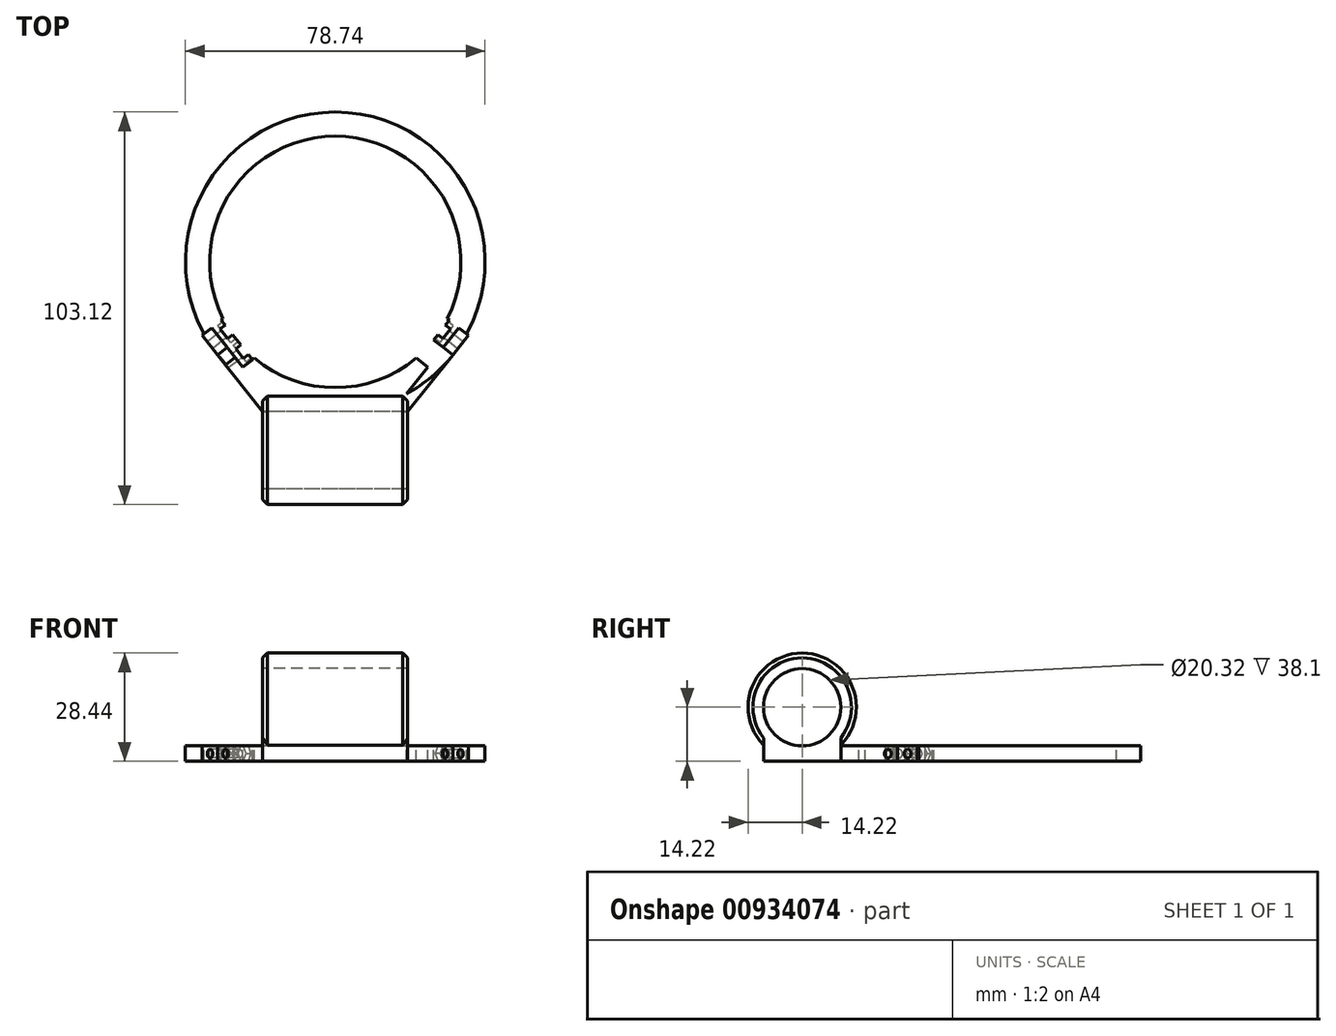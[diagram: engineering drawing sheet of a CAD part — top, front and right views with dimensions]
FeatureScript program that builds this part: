
annotation { "Feature Type Name" : "Feature", "Feature Type Description" : "" }
export const myFeature = defineFeature(function(context is Context, id is Id, definition is map)
    precondition{}
    {
        {
            var Q0;
            Q0=qCreatedBy(makeId("Top.planeOp"),FACE);
            var sketch = newSketch(context, id + "F0", { "sketchPlane" : qUnion([Q0])});
            skCircle(sketch, "E0", {"center": v(0, 0) * mm, "radius": 33.02 * mm});
            skCircle(sketch, "E1", {"center": v(0, 0) * mm, "radius": 39.37 * mm});
            skLineSegment(sketch, "E2", {"start": v(0, -39.37) * mm, "end": v(0, -59.7) * mm});
            skLineSegment(sketch, "E3", {"start": v(0, -59.7) * mm, "end": v(-19.05, -59.7) * mm});
            skLineSegment(sketch, "E4.bottom", {"start": v(-19.05, -59.7) * mm, "end": v(19.05, -59.7) * mm});
            skLineSegment(sketch, "E4.top", {"start": v(-19.05, -39.37) * mm, "end": v(19.05, -39.37) * mm});
            skLineSegment(sketch, "E4.left", {"start": v(-19.05, -59.7) * mm, "end": v(-19.05, -39.37) * mm});
            skLineSegment(sketch, "E4.right", {"start": v(19.05, -59.7) * mm, "end": v(19.05, -39.37) * mm});
            skPoint(sketch, "E4.middle", {"position": v(0, -49.53) * mm});
            skLineSegment(sketch, "E5", {"start": v(-19.05, -39.37) * mm, "end": v(-30.87, -24.43) * mm});
            skLineSegment(sketch, "E6", {"start": v(19.05, -39.37) * mm, "end": v(30.87, -24.43) * mm});
            skLineSegment(sketch, "E7", {"start": v(-30.87, -24.43) * mm, "end": v(-25.9, -20.5) * mm});
            skLineSegment(sketch, "E8", {"start": v(30.87, -24.43) * mm, "end": v(25.9, -20.5) * mm});
            skLineSegment(sketch, "E9", {"start": v(25.9, -20.5) * mm, "end": v(10.95, -39.37) * mm});
            skLineSegment(sketch, "E10", {"start": v(-25.9, -20.5) * mm, "end": v(-10.95, -39.37) * mm});
            skLineSegment(sketch, "E11", {"start": v(-28.38, -22.46) * mm, "end": v(-15, -39.37) * mm});
            skLineSegment(sketch, "E12", {"start": v(28.38, -22.46) * mm, "end": v(15, -39.37) * mm});
            skLineSegment(sketch, "E13", {"start": v(28.38, -22.46) * mm, "end": v(29.17, -21.47) * mm});
            skLineSegment(sketch, "E14", {"start": v(28.38, -22.46) * mm, "end": v(27.6, -23.46) * mm});
            skLineSegment(sketch, "E15", {"start": v(27.6, -23.46) * mm, "end": v(25.07, -26.64) * mm});
            skLineSegment(sketch, "E16", {"start": v(25.07, -26.64) * mm, "end": v(24.28, -27.64) * mm});
            skLineSegment(sketch, "E17", {"start": v(29.17, -21.47) * mm, "end": v(31.7, -18.28) * mm});
            skLineSegment(sketch, "E18", {"start": v(31.7, -18.28) * mm, "end": v(32.48, -17.28) * mm});
            skLineSegment(sketch, "E19", {"start": v(32.48, -17.28) * mm, "end": v(34.53, -18.9) * mm});
            skLineSegment(sketch, "E20", {"start": v(30.43, -19.87) * mm, "end": v(32.81, -21.76) * mm});
            skLineSegment(sketch, "E21", {"start": v(24.28, -27.64) * mm, "end": v(21.27, -25.26) * mm});
            skLineSegment(sketch, "E22", {"start": v(21.27, -25.26) * mm, "end": v(-21.27, -25.26) * mm});
            skLineSegment(sketch, "E23", {"start": v(-21.27, -25.26) * mm, "end": v(-24.28, -27.64) * mm});
            skLineSegment(sketch, "E24", {"start": v(-28.38, -22.46) * mm, "end": v(-32.48, -17.28) * mm});
            skLineSegment(sketch, "E25", {"start": v(-32.48, -17.28) * mm, "end": v(-34.53, -18.9) * mm});
            skLineSegment(sketch, "E26", {"start": v(-30.43, -19.87) * mm, "end": v(-32.81, -21.76) * mm});
            skLineSegment(sketch, "E27", {"start": v(-24.28, -27.64) * mm, "end": v(-28.38, -22.46) * mm});
            skLineSegment(sketch, "E28", {"start": v(-26.33, -25.05) * mm, "end": v(-28.82, -27.02) * mm});
            skLineSegment(sketch, "E29", {"start": v(26.33, -25.05) * mm, "end": v(28.82, -27.02) * mm});
            skLineSegment(sketch, "E30", {"start": v(-30.87, -24.43) * mm, "end": v(-34.97, -19.25) * mm});
            skLineSegment(sketch, "E31", {"start": v(-34.97, -19.25) * mm, "end": v(-32.48, -17.28) * mm});
            skLineSegment(sketch, "E32", {"start": v(30.87, -24.43) * mm, "end": v(34.97, -19.25) * mm});
            skLineSegment(sketch, "E33", {"start": v(34.97, -19.25) * mm, "end": v(32.48, -17.28) * mm});
            skLineSegment(sketch, "E34", {"start": v(-25.9, -20.5) * mm, "end": v(-21.8, -25.67) * mm});
            skLineSegment(sketch, "E35", {"start": v(-25.9, -20.5) * mm, "end": v(-30, -15.31) * mm});
            skLineSegment(sketch, "E36", {"start": v(-30, -15.31) * mm, "end": v(-29.47, -14.9) * mm});
            skLineSegment(sketch, "E37", {"start": v(25.9, -20.5) * mm, "end": v(30, -15.31) * mm});
            skLineSegment(sketch, "E38", {"start": v(30, -15.31) * mm, "end": v(29.47, -14.9) * mm});
            skSolve(sketch);
        }
        {
            var Q0;
            {var subQ8=sQuery(id+"F0.wireOp",EDGE,"E13");Q0=makeQuery(id+"F0.imprint","IMPRINT",FACE,{"disambiguationData":[TD([[makeQuery(id+"F0.imprint","IMPRINT",EDGE,{"derivedFrom":subQ8}),1.0]])]});}
            var Q1;
            {var subQ1=sQuery(id+"F0.wireOp",EDGE,"E23");var subQ4=sQuery(id+"F0.wireOp",EDGE,"E10");var subQ5=makeQuery(id+"F0.imprint","INTERSECT",VERTEX,{"derivedFrom":[subQ4,subQ1]});Q1=makeQuery(id+"F0.imprint","IMPRINT",FACE,{"disambiguationData":[TD([[makeQuery(id+"F0.imprint","IMPRINT",EDGE,{"disambiguationData":[TD([[subQ5,1.0]])],"derivedFrom":subQ4}),-1.0]])]});}
            var Q2;
            {var subQ1=sQuery(id+"F0.wireOp",EDGE,"E14");Q2=makeQuery(id+"F0.imprint","IMPRINT",FACE,{"disambiguationData":[TD([[makeQuery(id+"F0.imprint","IMPRINT",EDGE,{"derivedFrom":subQ1}),-1.0]])]});}
            var Q3;
            {var subQ6=sQuery(id+"F0.wireOp",EDGE,"E34");Q3=makeQuery(id+"F0.imprint","IMPRINT",FACE,{"disambiguationData":[TD([[makeQuery(id+"F0.imprint","IMPRINT",EDGE,{"derivedFrom":subQ6}),-1.0]])]});}
            extrude(context, id + "F1", {"entities" : qUnion([Q0, Q1, Q2, Q3]), "oppositeDirection" : true, "depth" : 4.06 * mm, "offsetDistance" : 25.4 * mm});
        }
        {
            var Q0;
            {var subQ5=sQuery(id+"F0.wireOp",EDGE,"E2");Q0=makeQuery(id+"F0.imprint","IMPRINT",FACE,{"disambiguationData":[TD([[makeQuery(id+"F0.imprint","IMPRINT",EDGE,{"derivedFrom":subQ5}),-1.0]])]});}
            var Q1;
            {var subQ1=sQuery(id+"F0.wireOp",EDGE,"E2");Q1=makeQuery(id+"F0.imprint","IMPRINT",FACE,{"disambiguationData":[TD([[makeQuery(id+"F0.imprint","IMPRINT",EDGE,{"derivedFrom":subQ1}),1.0]])]});}
            var Q2;
            {var subQ3=sQuery(id+"F0.wireOp",EDGE,"E1");var subQ7=sQuery(id+"F0.wireOp",EDGE,"E28");var subQ9=makeQuery(id+"F0.imprint","INTERSECT",VERTEX,{"derivedFrom":[subQ3,subQ7]});Q2=makeQuery(id+"F0.imprint","IMPRINT",FACE,{"disambiguationData":[TD([[makeQuery(id+"F0.imprint","IMPRINT",EDGE,{"disambiguationData":[TD([[subQ9,-1.0]])],"derivedFrom":subQ3}),-1.0]])]});}
            var Q3;
            {var subQ0=sQuery(id+"F0.wireOp",EDGE,"E11");var subQ1=sQuery(id+"F0.wireOp",EDGE,"E1");var subQ2=makeQuery(id+"F0.imprint","INTERSECT",VERTEX,{"derivedFrom":[subQ1,subQ0]});Q3=makeQuery(id+"F0.imprint","IMPRINT",FACE,{"disambiguationData":[TD([[makeQuery(id+"F0.imprint","IMPRINT",EDGE,{"disambiguationData":[TD([[subQ2,-1.0]])],"derivedFrom":subQ1}),-1.0]])]});}
            var Q4;
            {var subQ0=sQuery(id+"F0.wireOp",EDGE,"E4.top");var subQ3=sQuery(id+"F0.wireOp",EDGE,"E10");var subQ5=makeQuery(id+"F0.imprint","INTERSECT",VERTEX,{"derivedFrom":[subQ0,subQ3]});Q4=makeQuery(id+"F0.imprint","IMPRINT",FACE,{"disambiguationData":[TD([[makeQuery(id+"F0.imprint","IMPRINT",EDGE,{"disambiguationData":[TD([[subQ5,1.0]])],"derivedFrom":subQ3}),1.0]])]});}
            var Q5;
            {var subQ0=sQuery(id+"F0.wireOp",EDGE,"E9");var subQ1=sQuery(id+"F0.wireOp",EDGE,"E1");var subQ2=makeQuery(id+"F0.imprint","INTERSECT",VERTEX,{"derivedFrom":[subQ1,subQ0]});Q5=makeQuery(id+"F0.imprint","IMPRINT",FACE,{"disambiguationData":[TD([[makeQuery(id+"F0.imprint","IMPRINT",EDGE,{"disambiguationData":[TD([[subQ2,1.0]])],"derivedFrom":subQ0}),-1.0]])]});}
            var Q6;
            {var subQ0=sQuery(id+"F0.wireOp",EDGE,"E9");var subQ1=sQuery(id+"F0.wireOp",EDGE,"E1");var subQ2=makeQuery(id+"F0.imprint","INTERSECT",VERTEX,{"derivedFrom":[subQ1,subQ0]});Q6=makeQuery(id+"F0.imprint","IMPRINT",FACE,{"disambiguationData":[TD([[makeQuery(id+"F0.imprint","IMPRINT",EDGE,{"disambiguationData":[TD([[subQ2,-1.0]])],"derivedFrom":subQ1}),1.0]])]});}
            var Q7;
            {var subQ0=sQuery(id+"F0.wireOp",EDGE,"E4.top");var subQ3=sQuery(id+"F0.wireOp",EDGE,"E9");var subQ5=makeQuery(id+"F0.imprint","INTERSECT",VERTEX,{"derivedFrom":[subQ0,subQ3]});Q7=makeQuery(id+"F0.imprint","IMPRINT",FACE,{"disambiguationData":[TD([[makeQuery(id+"F0.imprint","IMPRINT",EDGE,{"disambiguationData":[TD([[subQ5,1.0]])],"derivedFrom":subQ3}),-1.0]])]});}
            var Q8;
            {var subQ0=sQuery(id+"F0.wireOp",EDGE,"E9");var subQ1=sQuery(id+"F0.wireOp",EDGE,"E1");var subQ2=makeQuery(id+"F0.imprint","INTERSECT",VERTEX,{"derivedFrom":[subQ1,subQ0]});Q8=makeQuery(id+"F0.imprint","IMPRINT",FACE,{"disambiguationData":[TD([[makeQuery(id+"F0.imprint","IMPRINT",EDGE,{"disambiguationData":[TD([[subQ2,-1.0]])],"derivedFrom":subQ1}),-1.0]])]});}
            var Q9;
            {var subQ0=sQuery(id+"F0.wireOp",EDGE,"E12");var subQ3=sQuery(id+"F0.wireOp",EDGE,"E1");var subQ4=makeQuery(id+"F0.imprint","INTERSECT",VERTEX,{"derivedFrom":[subQ3,subQ0]});Q9=makeQuery(id+"F0.imprint","IMPRINT",FACE,{"disambiguationData":[TD([[makeQuery(id+"F0.imprint","IMPRINT",EDGE,{"disambiguationData":[TD([[subQ4,-1.0]])],"derivedFrom":subQ3}),-1.0]])]});}
            var Q10;
            {var subQ0=sQuery(id+"F0.wireOp",EDGE,"E16");Q10=makeQuery(id+"F0.imprint","IMPRINT",FACE,{"disambiguationData":[TD([[makeQuery(id+"F0.imprint","IMPRINT",EDGE,{"derivedFrom":subQ0}),1.0]])]});}
            var Q11;
            {var subQ0=sQuery(id+"F0.wireOp",EDGE,"E6");var subQ3=sQuery(id+"F0.wireOp",EDGE,"E29");var subQ5=makeQuery(id+"F0.imprint","INTERSECT",VERTEX,{"derivedFrom":[subQ0,subQ3]});Q11=makeQuery(id+"F0.imprint","IMPRINT",FACE,{"disambiguationData":[TD([[makeQuery(id+"F0.imprint","IMPRINT",EDGE,{"disambiguationData":[TD([[subQ5,1.0]])],"derivedFrom":subQ3}),1.0]])]});}
            var Q12;
            {var subQ0=sQuery(id+"F0.wireOp",EDGE,"E14");Q12=makeQuery(id+"F0.imprint","IMPRINT",FACE,{"disambiguationData":[TD([[makeQuery(id+"F0.imprint","IMPRINT",EDGE,{"derivedFrom":subQ0}),1.0]])]});}
            var Q13;
            {var subQ1=sQuery(id+"F0.wireOp",EDGE,"E13");Q13=makeQuery(id+"F0.imprint","IMPRINT",FACE,{"disambiguationData":[TD([[makeQuery(id+"F0.imprint","IMPRINT",EDGE,{"derivedFrom":subQ1}),-1.0]])]});}
            var Q14;
            {var subQ1=sQuery(id+"F0.wireOp",EDGE,"E18");Q14=makeQuery(id+"F0.imprint","IMPRINT",FACE,{"disambiguationData":[TD([[makeQuery(id+"F0.imprint","IMPRINT",EDGE,{"derivedFrom":subQ1}),-1.0]])]});}
            var Q15;
            {var subQ0=sQuery(id+"F0.wireOp",EDGE,"E11");var subQ1=sQuery(id+"F0.wireOp",EDGE,"E1");var subQ2=makeQuery(id+"F0.imprint","INTERSECT",VERTEX,{"derivedFrom":[subQ1,subQ0]});Q15=makeQuery(id+"F0.imprint","IMPRINT",FACE,{"disambiguationData":[TD([[makeQuery(id+"F0.imprint","IMPRINT",EDGE,{"disambiguationData":[TD([[subQ2,-1.0]])],"derivedFrom":subQ1}),1.0]])]});}
            var Q16;
            {var subQ0=sQuery(id+"F0.wireOp",EDGE,"E5");var subQ3=sQuery(id+"F0.wireOp",EDGE,"E28");var subQ5=makeQuery(id+"F0.imprint","INTERSECT",VERTEX,{"derivedFrom":[subQ0,subQ3]});Q16=makeQuery(id+"F0.imprint","IMPRINT",FACE,{"disambiguationData":[TD([[makeQuery(id+"F0.imprint","IMPRINT",EDGE,{"disambiguationData":[TD([[subQ5,1.0]])],"derivedFrom":subQ3}),-1.0]])]});}
            var Q17;
            {var subQ0=sQuery(id+"F0.wireOp",EDGE,"E28");var subQ1=sQuery(id+"F0.wireOp",EDGE,"E1");var subQ2=makeQuery(id+"F0.imprint","INTERSECT",VERTEX,{"derivedFrom":[subQ1,subQ0]});Q17=makeQuery(id+"F0.imprint","IMPRINT",FACE,{"disambiguationData":[TD([[makeQuery(id+"F0.imprint","IMPRINT",EDGE,{"disambiguationData":[TD([[subQ2,-1.0]])],"derivedFrom":subQ1}),1.0]])]});}
            var Q18;
            {var subQ3=sQuery(id+"F0.wireOp",EDGE,"E28");var subQ5=sQuery(id+"F0.wireOp",EDGE,"E27");var subQ7=makeQuery(id+"F0.imprint","INTERSECT",VERTEX,{"derivedFrom":[subQ5,subQ3]});Q18=makeQuery(id+"F0.imprint","IMPRINT",FACE,{"disambiguationData":[TD([[makeQuery(id+"F0.imprint","IMPRINT",EDGE,{"disambiguationData":[TD([[subQ7,-1.0]])],"derivedFrom":subQ3}),-1.0]])]});}
            var Q19;
            {var subQ3=sQuery(id+"F0.wireOp",EDGE,"E26");Q19=makeQuery(id+"F0.imprint","IMPRINT",FACE,{"disambiguationData":[TD([[makeQuery(id+"F0.imprint","IMPRINT",EDGE,{"derivedFrom":subQ3}),1.0]])]});}
            var Q20;
            {var subQ0=sQuery(id+"F0.wireOp",EDGE,"E25");Q20=makeQuery(id+"F0.imprint","IMPRINT",FACE,{"disambiguationData":[TD([[makeQuery(id+"F0.imprint","IMPRINT",EDGE,{"derivedFrom":subQ0}),1.0]])]});}
            var Q21;
            {var subQ0=sQuery(id+"F0.wireOp",EDGE,"E32");Q21=makeQuery(id+"F0.imprint","IMPRINT",FACE,{"disambiguationData":[TD([[makeQuery(id+"F0.imprint","IMPRINT",EDGE,{"derivedFrom":subQ0}),1.0]])]});}
            var Q22;
            {var subQ0=sQuery(id+"F0.wireOp",EDGE,"E26");Q22=makeQuery(id+"F0.imprint","IMPRINT",FACE,{"disambiguationData":[TD([[makeQuery(id+"F0.imprint","IMPRINT",EDGE,{"derivedFrom":subQ0}),-1.0]])]});}
            var Q23;
            {var subQ4=sQuery(id+"F0.wireOp",EDGE,"E30");Q23=makeQuery(id+"F0.imprint","IMPRINT",FACE,{"disambiguationData":[TD([[makeQuery(id+"F0.imprint","IMPRINT",EDGE,{"derivedFrom":subQ4}),-1.0]])]});}
            extrude(context, id + "F2", {"entities" : qUnion([Q0, Q1, Q2, Q3, Q4, Q5, Q6, Q7, Q8, Q9, Q10, Q11, Q12, Q13, Q14, Q15, Q16, Q17, Q18, Q19, Q20, Q21, Q22, Q23]), "oppositeDirection" : true, "depth" : 4.06 * mm, "offsetDistance" : 25.4 * mm});
        }
        {
            var Q0;
            Q0=makeQuery(id+"F1.opExtrude","SWEPT_FACE",FACE,{"disambiguationData":[OSD([sQuery(id+"F0.wireOp",EDGE,"E24"),sQuery(id+"F0.wireOp",EDGE,"E27")])]});
            var sketch = newSketch(context, id + "F3", { "sketchPlane" : qUnion([Q0])});
            skLineSegment(sketch, "E39", {"start": v(0, 0) * mm, "end": v(0, -4.06) * mm});
            skLineSegment(sketch, "E40", {"start": v(0, -4.06) * mm, "end": v(-6.6, -4.06) * mm});
            skLineSegment(sketch, "E41", {"start": v(0, -4.06) * mm, "end": v(6.6, -4.06) * mm});
            skLineSegment(sketch, "E42", {"start": v(-3.3, -4.06) * mm, "end": v(-3.3, -2.03) * mm});
            skLineSegment(sketch, "E43", {"start": v(3.3, -4.06) * mm, "end": v(3.3, -2.03) * mm});
            skCircle(sketch, "E44", {"center": v(-3.3, -2.03) * mm, "radius": 1.14 * mm});
            skCircle(sketch, "E45", {"center": v(3.3, -2.03) * mm, "radius": 1.14 * mm});
            skSolve(sketch);
        }
        {
            var Q0;
            Q0=makeQuery(id+"F3.imprint","IMPRINT",FACE,{"disambiguationData":[TD([[makeQuery(id+"F3.imprint","IMPRINT",EDGE,{"derivedFrom":sQuery(id+"F3.wireOp",EDGE,"E44")}),1.0]])]});
            var Q1;
            Q1=makeQuery(id+"F3.imprint","IMPRINT",FACE,{"disambiguationData":[TD([[makeQuery(id+"F3.imprint","IMPRINT",EDGE,{"derivedFrom":sQuery(id+"F3.wireOp",EDGE,"E45")}),1.0]])]});
            extrude(context, id + "F4", {"entities" : qUnion([Q0, Q1]), "operationType" : NewBodyOperationType.REMOVE, "endBound" : BoundingType.SYMMETRIC, "oppositeDirection" : true, "depth" : 25.4 * mm, "offsetDistance" : 25.4 * mm});
        }
        {
            var Q0;
            Q0=makeQuery(id+"F1.opExtrude","SWEPT_FACE",FACE,{"disambiguationData":[OSD([sQuery(id+"F0.wireOp",EDGE,"E13"),sQuery(id+"F0.wireOp",EDGE,"E14"),sQuery(id+"F0.wireOp",EDGE,"E15"),sQuery(id+"F0.wireOp",EDGE,"E16"),sQuery(id+"F0.wireOp",EDGE,"E17"),sQuery(id+"F0.wireOp",EDGE,"E18")])]});
            var sketch = newSketch(context, id + "F5", { "sketchPlane" : qUnion([Q0])});
            skLineSegment(sketch, "E46", {"start": v(0, 0) * mm, "end": v(0, -4.06) * mm});
            skLineSegment(sketch, "E47", {"start": v(0, 0) * mm, "end": v(-3.3, 0) * mm});
            skLineSegment(sketch, "E48", {"start": v(0, -2.03) * mm, "end": v(-3.3, -2.03) * mm});
            skLineSegment(sketch, "E49", {"start": v(0, -2.03) * mm, "end": v(3.3, -2.03) * mm});
            skCircle(sketch, "E50", {"center": v(-3.3, -2.03) * mm, "radius": 1.14 * mm});
            skCircle(sketch, "E51", {"center": v(3.3, -2.03) * mm, "radius": 1.14 * mm});
            skSolve(sketch);
        }
        {
            var Q0;
            Q0=makeQuery(id+"F5.imprint","IMPRINT",FACE,{"disambiguationData":[TD([[makeQuery(id+"F5.imprint","IMPRINT",EDGE,{"derivedFrom":sQuery(id+"F5.wireOp",EDGE,"E50")}),1.0]])]});
            var Q1;
            Q1=makeQuery(id+"F5.imprint","IMPRINT",FACE,{"disambiguationData":[TD([[makeQuery(id+"F5.imprint","IMPRINT",EDGE,{"derivedFrom":sQuery(id+"F5.wireOp",EDGE,"E51")}),1.0]])]});
            extrude(context, id + "F6", {"entities" : qUnion([Q0, Q1]), "operationType" : NewBodyOperationType.REMOVE, "endBound" : BoundingType.SYMMETRIC, "oppositeDirection" : true, "depth" : 25.4 * mm, "offsetDistance" : 25.4 * mm});
        }
        {
            var Q0;
            Q0=makeQuery(id+"F1.opExtrude","SWEPT_FACE",FACE,{"disambiguationData":[OSD([sQuery(id+"F0.wireOp",EDGE,"E34"),sQuery(id+"F0.wireOp",EDGE,"E35")])]});
            var sketch = newSketch(context, id + "F7", { "sketchPlane" : qUnion([Q0])});
            skLineSegment(sketch, "E52", {"start": v(3.3, -2.03) * mm, "end": v(5.72, -2.03) * mm});
            skLineSegment(sketch, "E53", {"start": v(3.3, -2.03) * mm, "end": v(3.3, -4.45) * mm});
            skCircle(sketch, "E54.cCircle", {"center": v(3.3, -2.03) * mm, "radius": 2.41 * mm, "construction": true});
            skLineSegment(sketch, "E54.0", {"start": v(4.7, -4.45) * mm, "end": v(1.9, -4.45) * mm});
            skLineSegment(sketch, "E54.1", {"start": v(1.9, -4.45) * mm, "end": v(0.52, -2.03) * mm});
            skLineSegment(sketch, "E54.2", {"start": v(0.52, -2.03) * mm, "end": v(1.9, 0.38) * mm});
            skLineSegment(sketch, "E54.3", {"start": v(1.9, 0.38) * mm, "end": v(4.7, 0.38) * mm});
            skLineSegment(sketch, "E54.4", {"start": v(4.7, 0.38) * mm, "end": v(6.09, -2.03) * mm});
            skLineSegment(sketch, "E54.5", {"start": v(6.09, -2.03) * mm, "end": v(4.7, -4.45) * mm});
            skPoint(sketch, "E54.0.midPoint", {"position": v(3.3, -4.45) * mm});
            skCircle(sketch, "E55.cCircle", {"center": v(-3.3, -2.03) * mm, "radius": 2.41 * mm, "construction": true});
            skLineSegment(sketch, "E55.0", {"start": v(-1.9, -4.45) * mm, "end": v(-4.7, -4.45) * mm});
            skLineSegment(sketch, "E55.1", {"start": v(-4.7, -4.45) * mm, "end": v(-6.09, -2.03) * mm});
            skLineSegment(sketch, "E55.2", {"start": v(-6.09, -2.03) * mm, "end": v(-4.7, 0.38) * mm});
            skLineSegment(sketch, "E55.3", {"start": v(-4.7, 0.38) * mm, "end": v(-1.9, 0.38) * mm});
            skLineSegment(sketch, "E55.4", {"start": v(-1.9, 0.38) * mm, "end": v(-0.52, -2.03) * mm});
            skLineSegment(sketch, "E55.5", {"start": v(-0.52, -2.03) * mm, "end": v(-1.9, -4.45) * mm});
            skPoint(sketch, "E55.0.midPoint", {"position": v(-3.3, -4.45) * mm});
            skSolve(sketch);
        }
        {
            var Q0;
            {var subQ7=sQuery(id+"F7.wireOp",EDGE,"E54.2");var subQ8=sQuery(id+"F7.wireOp",EDGE,"E54.1");var subQ9=makeQuery(id+"F7.imprint","INTERSECT",VERTEX,{"derivedFrom":[subQ8,subQ7]});Q0=makeQuery(id+"F7.imprint","IMPRINT",FACE,{"disambiguationData":[TD([[makeQuery(id+"F7.imprint","IMPRINT",EDGE,{"disambiguationData":[TD([[subQ9,1.0]])],"derivedFrom":subQ8}),-1.0]])]});}
            var Q1;
            {var subQ3=sQuery(id+"F0.wireOp",EDGE,"E35");var subQ4=sQuery(id+"F0.wireOp",EDGE,"E34");Q1=makeQuery(id+"F7.imprint","IMPRINT",FACE,{"disambiguationData":[TD([[makeQuery(id+"F7.imprint","IMPRINT",EDGE,{"derivedFrom":makeQuery(id+"F4.boolean.opBoolean","INTERSECT",EDGE,{"derivedFrom":[makeQuery(id+"F1.opExtrude","SWEPT_FACE",FACE,{"disambiguationData":[OSD([subQ4,subQ3])]}),makeQuery(id+"F4.opExtrude","SWEPT_FACE",FACE,{"disambiguationData":[OSD([sQuery(id+"F3.wireOp",EDGE,"E45")])]})]})}),-1.0]])]});}
            extrude(context, id + "F8", {"entities" : qUnion([Q0, Q1]), "operationType" : NewBodyOperationType.REMOVE, "oppositeDirection" : true, "depth" : 1.65 * mm, "offsetDistance" : 25.4 * mm});
        }
        {
            var Q0;
            Q0=makeQuery(id+"F1.opExtrude","SWEPT_FACE",FACE,{"disambiguationData":[OSD([sQuery(id+"F0.wireOp",EDGE,"E9"),sQuery(id+"F0.wireOp",EDGE,"E37")])]});
            var sketch = newSketch(context, id + "F9", { "sketchPlane" : qUnion([Q0])});
            skCircle(sketch, "E56.cCircle", {"center": v(-3.3, -2.03) * mm, "radius": 2.41 * mm, "construction": true});
            skLineSegment(sketch, "E56.0", {"start": v(-4.7, 0.38) * mm, "end": v(-1.9, 0.38) * mm});
            skLineSegment(sketch, "E56.1", {"start": v(-1.9, 0.38) * mm, "end": v(-0.52, -2.03) * mm});
            skLineSegment(sketch, "E56.2", {"start": v(-0.52, -2.03) * mm, "end": v(-1.9, -4.45) * mm});
            skLineSegment(sketch, "E56.3", {"start": v(-1.9, -4.45) * mm, "end": v(-4.7, -4.45) * mm});
            skLineSegment(sketch, "E56.4", {"start": v(-4.7, -4.45) * mm, "end": v(-6.09, -2.03) * mm});
            skLineSegment(sketch, "E56.5", {"start": v(-6.09, -2.03) * mm, "end": v(-4.7, 0.38) * mm});
            skPoint(sketch, "E56.0.midPoint", {"position": v(-3.3, 0.38) * mm});
            skCircle(sketch, "E57.cCircle", {"center": v(3.3, -2.03) * mm, "radius": 2.41 * mm, "construction": true});
            skLineSegment(sketch, "E57.0", {"start": v(1.9, 0.38) * mm, "end": v(4.7, 0.38) * mm});
            skLineSegment(sketch, "E57.1", {"start": v(4.7, 0.38) * mm, "end": v(6.09, -2.03) * mm});
            skLineSegment(sketch, "E57.2", {"start": v(6.09, -2.03) * mm, "end": v(4.7, -4.45) * mm});
            skLineSegment(sketch, "E57.3", {"start": v(4.7, -4.45) * mm, "end": v(1.9, -4.45) * mm});
            skLineSegment(sketch, "E57.4", {"start": v(1.9, -4.45) * mm, "end": v(0.52, -2.03) * mm});
            skLineSegment(sketch, "E57.5", {"start": v(0.52, -2.03) * mm, "end": v(1.9, 0.38) * mm});
            skPoint(sketch, "E57.0.midPoint", {"position": v(3.3, 0.38) * mm});
            skSolve(sketch);
        }
        {
            var Q0;
            {var subQ3=sQuery(id+"F0.wireOp",EDGE,"E37");var subQ4=sQuery(id+"F0.wireOp",EDGE,"E9");Q0=makeQuery(id+"F9.imprint","IMPRINT",FACE,{"disambiguationData":[TD([[makeQuery(id+"F9.imprint","IMPRINT",EDGE,{"derivedFrom":makeQuery(id+"F6.boolean.opBoolean","INTERSECT",EDGE,{"derivedFrom":[makeQuery(id+"F1.opExtrude","SWEPT_FACE",FACE,{"disambiguationData":[OSD([subQ4,subQ3])]}),makeQuery(id+"F6.opExtrude","SWEPT_FACE",FACE,{"disambiguationData":[OSD([sQuery(id+"F5.wireOp",EDGE,"E51")])]})]})}),1.0]])]});}
            var Q1;
            {var subQ3=sQuery(id+"F0.wireOp",EDGE,"E37");var subQ4=sQuery(id+"F0.wireOp",EDGE,"E9");Q1=makeQuery(id+"F9.imprint","IMPRINT",FACE,{"disambiguationData":[TD([[makeQuery(id+"F9.imprint","IMPRINT",EDGE,{"derivedFrom":makeQuery(id+"F6.boolean.opBoolean","INTERSECT",EDGE,{"derivedFrom":[makeQuery(id+"F1.opExtrude","SWEPT_FACE",FACE,{"disambiguationData":[OSD([subQ4,subQ3])]}),makeQuery(id+"F6.opExtrude","SWEPT_FACE",FACE,{"disambiguationData":[OSD([sQuery(id+"F5.wireOp",EDGE,"E50")])]})]})}),1.0]])]});}
            extrude(context, id + "F10", {"entities" : qUnion([Q0, Q1]), "operationType" : NewBodyOperationType.REMOVE, "oppositeDirection" : true, "depth" : 1.65 * mm, "offsetDistance" : 25.4 * mm});
        }
        {
            var Q0;
            Q0=qCreatedBy(makeId("Right.planeOp"),FACE);
            var sketch = newSketch(context, id + "F11", { "sketchPlane" : qUnion([Q0])});
            skLineSegment(sketch, "E58", {"start": v(0, 0) * mm, "end": v(-59.7, 0) * mm});
            skLineSegment(sketch, "E59", {"start": v(-59.7, 0) * mm, "end": v(-39.37, 0) * mm});
            skLineSegment(sketch, "E60", {"start": v(-49.53, 0) * mm, "end": v(-49.53, 10.16) * mm});
            skCircle(sketch, "E61", {"center": v(-49.53, 10.16) * mm, "radius": 10.16 * mm});
            skLineSegment(sketch, "E62", {"start": v(-49.53, 0) * mm, "end": v(-49.53, -4.06) * mm});
            skCircle(sketch, "E63", {"center": v(-49.53, 10.16) * mm, "radius": 14.22 * mm});
            skLineSegment(sketch, "E64", {"start": v(-59.7, 0) * mm, "end": v(-59.7, 0.2) * mm});
            skLineSegment(sketch, "E65", {"start": v(-39.37, 0) * mm, "end": v(-39.37, 0.2) * mm});
            skSolve(sketch);
        }
        {
            var Q0;
            {var subQ0=sQuery(id+"F11.wireOp",EDGE,"E62");Q0=makeQuery(id+"F11.imprint","IMPRINT",FACE,{"disambiguationData":[TD([[makeQuery(id+"F11.imprint","IMPRINT",EDGE,{"derivedFrom":subQ0}),1.0]])]});}
            var Q1;
            {var subQ0=sQuery(id+"F11.wireOp",EDGE,"E62");Q1=makeQuery(id+"F11.imprint","IMPRINT",FACE,{"disambiguationData":[TD([[makeQuery(id+"F11.imprint","IMPRINT",EDGE,{"derivedFrom":subQ0}),-1.0]])]});}
            var Q2;
            {var subQ0=sQuery(id+"F11.wireOp",EDGE,"E61");Q2=makeQuery(id+"F11.imprint","IMPRINT",FACE,{"disambiguationData":[TD([[makeQuery(id+"F11.imprint","IMPRINT",EDGE,{"derivedFrom":subQ0}),-1.0]])]});}
            var Q3;
            {var subQ0=sQuery(id+"F11.wireOp",EDGE,"E65");Q3=makeQuery(id+"F11.imprint","IMPRINT",FACE,{"disambiguationData":[TD([[makeQuery(id+"F11.imprint","IMPRINT",EDGE,{"derivedFrom":subQ0}),1.0]])]});}
            var Q4;
            {var subQ0=sQuery(id+"F11.wireOp",EDGE,"E64");Q4=makeQuery(id+"F11.imprint","IMPRINT",FACE,{"disambiguationData":[TD([[makeQuery(id+"F11.imprint","IMPRINT",EDGE,{"derivedFrom":subQ0}),-1.0]])]});}
            extrude(context, id + "F12", {"entities" : qUnion([Q0, Q1, Q2, Q3, Q4]), "operationType" : NewBodyOperationType.ADD, "endBound" : BoundingType.SYMMETRIC, "depth" : 38.1 * mm, "offsetDistance" : 25.4 * mm});
        }
        {
            var Q0;
            {var subQ0=sQuery(id+"F11.wireOp",EDGE,"E63");Q0=makeQuery(id+"F12.opExtrude","CAP_EDGE",EDGE,{"disambiguationData":[OSD([subQ0]),TDD([makeQuery(id+"F11.imprint","IMPRINT",EDGE,{"disambiguationData":[TD([[makeQuery(id+"F11.imprint","INTERSECT",VERTEX,{"derivedFrom":[subQ0,sQuery(id+"F11.wireOp",EDGE,"E64")]}),1.0]])],"derivedFrom":subQ0})])],"isStart":true});}
            var Q1;
            {var subQ0=sQuery(id+"F11.wireOp",EDGE,"E63");Q1=makeQuery(id+"F12.opExtrude","CAP_EDGE",EDGE,{"disambiguationData":[OSD([subQ0]),TDD([makeQuery(id+"F11.imprint","IMPRINT",EDGE,{"disambiguationData":[TD([[makeQuery(id+"F11.imprint","INTERSECT",VERTEX,{"derivedFrom":[subQ0,sQuery(id+"F11.wireOp",EDGE,"E64")]}),1.0]])],"derivedFrom":subQ0})])],"isStart":false});}
            chamfer(context, id + "F13", {"entities" : qUnion([Q0, Q1]), "width" : 1.27 * mm, "tangentPropagation" : true});
        }
    });
